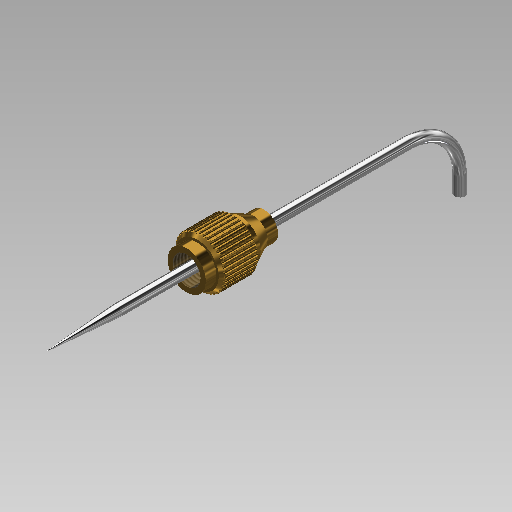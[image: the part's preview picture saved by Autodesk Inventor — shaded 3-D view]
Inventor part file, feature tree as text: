
AUTODESK INVENTOR PART (.ipt)
format: ipt  version: 2018.1 (Build 221171000, 171)  size: 409,600 bytes
history: native  units: in
note: dims shown in document units (in); Inventor stores cm internally (conversion verified against a paired STEP export)
features: sketch x8, extrude x4, chamfer x2, revolve x1, hole x1, thread x1, sweep x1
ambient origin geometry x8: Origin, YZ Plane, XZ Plane, XY Plane, X Axis, Y Axis, Z Axis, Center Point
bodies: Solid1 (feature_tree)
feature tree (18):
  extrude  "Extrusion1"  Depth=0.2205in TaperAngle=0.0deg
  extrude  "Extrusion2"  Depth=0.0591in
  revolve  "Revolution1"  Angle=90.0deg
  extrude  "Extrusion3"  Depth=0.0984in TaperAngle=0.0deg
  chamfer  "Chamfer1"  Distance=0.0394in Angle=45.0deg
  extrude  "Extrusion4"  Depth=0.0394in
  hole  "Hole1"  [1 undecoded]
  thread  "Thread1"  [1 undecoded]
  sweep  "Sweep1"
  chamfer  "Chamfer2"  [1 undecoded]
  sketch  "Sketch2"  dims[d14=15.748in d16=360.0deg d18=0.2205in d19=0.0in]
  sketch  "Sketch3"  dims[d21=0.0591in d22=0.0in d26=0.0957in]
  sketch  "Sketch4"  dims[d27=0.0502in d28=90.0deg]
  sketch  "Sketch5"  dims[d29=0.2362in d30=0.0984in d31=0.0in d32=0.0394in d33=0.0787in d34=45.0deg]
  sketch  "Sketch6"  dims[d35=0.0591in d36=0.0in d37=0.0394in]
  sketch  "Sketch7"  dims[d38=0.1575in d39=0.2362in d40=0.1575in d41=0.0787in d42=90.0deg d43=0.2362in d44=0.8108in d45=0.315in d46=0.0in d55=0.2953in]
  sketch  "3D Sketch1"
  sketch  "Sketch9"  dims[d57=0.0in d58=0.3937in d59=0.0276in d60=45.0deg d61=0.0in]
note: 3 required parameter values undecoded (feature->parameter linkage not recoverable at this tier; creation-order binding heuristic only, values carry confidence <= 0.55)
